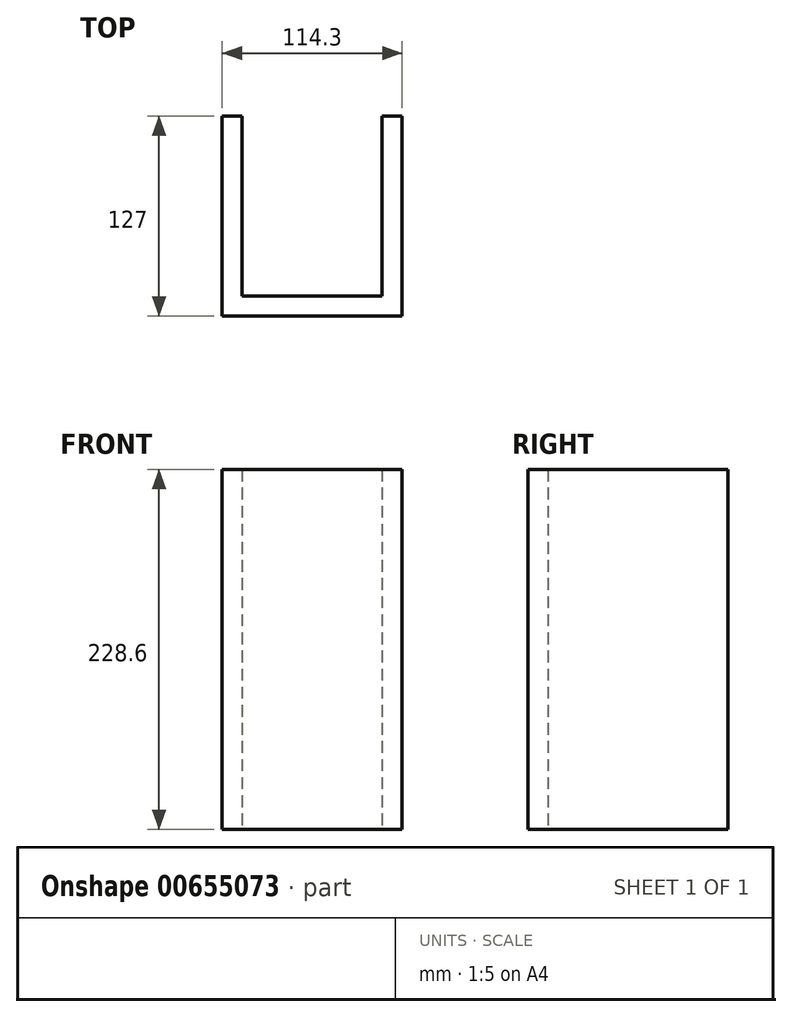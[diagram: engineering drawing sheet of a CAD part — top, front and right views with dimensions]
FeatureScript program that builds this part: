
annotation { "Feature Type Name" : "Feature", "Feature Type Description" : "" }
export const myFeature = defineFeature(function(context is Context, id is Id, definition is map)
    precondition{}
    {
        {
            var Q0;
            Q0=qCreatedBy(makeId("Right.planeOp"),FACE);
            var sketch = newSketch(context, id + "F0", { "sketchPlane" : qUnion([Q0])});
            skLineSegment(sketch, "E0.bottom", {"start": v(-63.5, 114.3) * mm, "end": v(63.5, 114.3) * mm});
            skLineSegment(sketch, "E0.top", {"start": v(-63.5, -114.3) * mm, "end": v(63.5, -114.3) * mm});
            skLineSegment(sketch, "E0.left", {"start": v(-63.5, 114.3) * mm, "end": v(-63.5, -114.3) * mm});
            skLineSegment(sketch, "E0.right", {"start": v(63.5, 114.3) * mm, "end": v(63.5, -114.3) * mm});
            skPoint(sketch, "E0.middle", {"position": v(0, 0) * mm});
            skSolve(sketch);
        }
        {
            var Q0;
            Q0=makeQuery(id+"F0.imprint","IMPRINT",FACE,{"disambiguationData":[TD([[makeQuery(id+"F0.imprint","IMPRINT",EDGE,{"derivedFrom":sQuery(id+"F0.wireOp",EDGE,"E0.bottom")}),-1.0]])]});
            extrude(context, id + "F1", {"entities" : qUnion([Q0]), "oppositeDirection" : true, "depth" : 12.7 * mm, "offsetDistance" : 25.4 * mm});
        }
        {
            var Q0;
            Q0=qCreatedBy(makeId("Right.planeOp"),FACE);
            cPlane(context, id + "F2", {"entities" : qUnion([Q0]), "cplaneType" : CPlaneType.OFFSET, "offset" : 101.6 * mm, "oppositeDirection" : true, "width" : 152.4 * mm, "height" : 152.4 * mm});
        }
        {
            var Q0;
            Q0=qCreatedBy(makeId("Front.planeOp"),FACE);
            cPlane(context, id + "F3", {"entities" : qUnion([Q0]), "cplaneType" : CPlaneType.OFFSET, "offset" : 50.8 * mm, "width" : 152.4 * mm, "height" : 152.4 * mm});
        }
        {
            var Q0;
            Q0=qCreatedBy(id+"F2.planeOp",FACE);
            var sketch = newSketch(context, id + "F4", { "sketchPlane" : qUnion([Q0])});
            skLineSegment(sketch, "E1.bottom", {"start": v(63.5, 114.3) * mm, "end": v(-63.5, 114.3) * mm});
            skLineSegment(sketch, "E1.top", {"start": v(63.5, -114.3) * mm, "end": v(-63.5, -114.3) * mm});
            skLineSegment(sketch, "E1.left", {"start": v(63.5, 114.3) * mm, "end": v(63.5, -114.3) * mm});
            skLineSegment(sketch, "E1.right", {"start": v(-63.5, 114.3) * mm, "end": v(-63.5, -114.3) * mm});
            skPoint(sketch, "E1.middle", {"position": v(0, 0) * mm});
            skSolve(sketch);
        }
        {
            var Q0;
            Q0 = qSketchRegion(id + "F4", true);
            extrude(context, id + "F5", {"entities" : qUnion([Q0]), "oppositeDirection" : true, "depth" : 12.7 * mm, "offsetDistance" : 25.4 * mm});
        }
        {
            var Q0;
            Q0=qCreatedBy(id+"F3.planeOp",FACE);
            var sketch = newSketch(context, id + "F6", { "sketchPlane" : qUnion([Q0])});
            skLineSegment(sketch, "E2.bottom", {"start": v(-106.54, 114.3) * mm, "end": v(-8.39, 114.3) * mm});
            skLineSegment(sketch, "E2.top", {"start": v(-106.54, -114.3) * mm, "end": v(-8.39, -114.3) * mm});
            skLineSegment(sketch, "E2.left", {"start": v(-106.54, 114.3) * mm, "end": v(-106.54, -114.3) * mm});
            skLineSegment(sketch, "E2.right", {"start": v(-8.39, 114.3) * mm, "end": v(-8.39, -114.3) * mm});
            skPoint(sketch, "E2.middle", {"position": v(-57.46, 0) * mm});
            skSolve(sketch);
        }
        {
            var Q0;
            Q0=makeQuery(id+"F6.imprint","IMPRINT",FACE,{"disambiguationData":[TD([[makeQuery(id+"F6.imprint","IMPRINT",EDGE,{"derivedFrom":sQuery(id+"F6.wireOp",EDGE,"E2.bottom")}),-1.0]])]});
            extrude(context, id + "F7", {"entities" : qUnion([Q0]), "operationType" : NewBodyOperationType.ADD, "depth" : 12.7 * mm, "offsetDistance" : 25.4 * mm});
        }
    });
